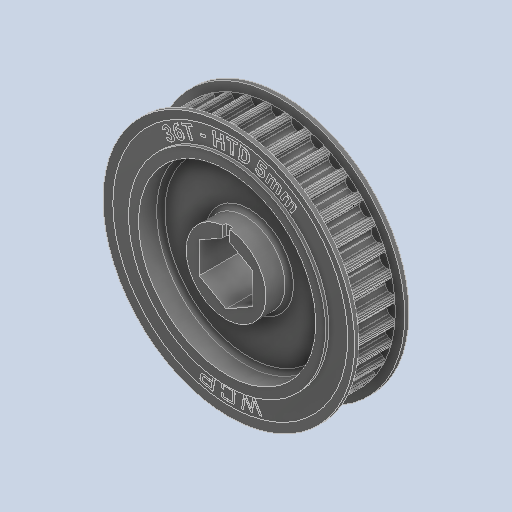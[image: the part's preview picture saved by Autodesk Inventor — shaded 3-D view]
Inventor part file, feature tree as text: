
AUTODESK INVENTOR PART (.ipt)
format: ipt  version: 2024 (Build 280153000, 153)  size: 1,094,144 bytes
history: native  units: in
note: dims shown in document units (in); Inventor stores cm internally (conversion verified against a paired STEP export)
features: mirror x2, other x1
ambient origin geometry x8: Origin, YZ Plane, XZ Plane, XY Plane, X Axis, Y Axis, Z Axis, Center Point
bodies: Solid1 (feature_tree), Solid2 (feature_tree), Solid3 (feature_tree)
feature tree (3):
  mirror  "Mirror1"
  mirror  "Mirror1:1"
  other  "Cut-Extrude5"
